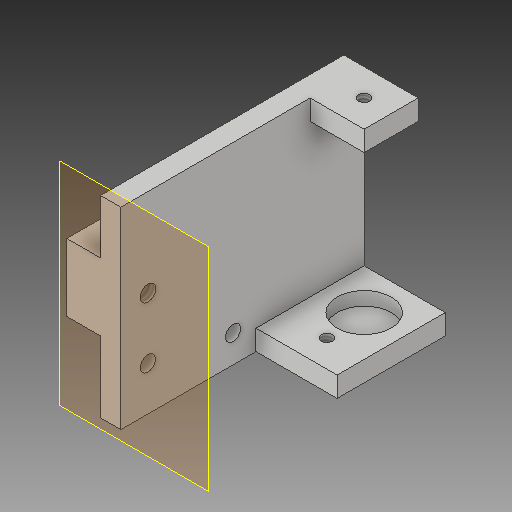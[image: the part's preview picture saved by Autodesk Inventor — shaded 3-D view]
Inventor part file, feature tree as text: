
AUTODESK INVENTOR PART (.ipt)
format: ipt  version: 2017 (Build 210142000, 142)  size: 203,776 bytes
history: native  units: in
note: dims shown in document units (in); Inventor stores cm internally (conversion verified against a paired STEP export)
features: projected_geometry x9, sketch x8, hole x5, extrude x4, plane x1, mirror x1
ambient origin geometry x8: Origin, YZ Plane, XZ Plane, XY Plane, X Axis, Y Axis, Z Axis, Center Point
bodies: Solid1 (feature_tree)
feature tree (28):
  extrude  "Extrusion1"  Depth=2.25in
  extrude  "Extrusion2"  Depth=0.5in
  extrude  "Extrusion3"  Depth=0.5in TaperAngle=0.0deg
  extrude  "Extrusion4"  Depth=0.75in TaperAngle=0.0deg
  hole  "Hole1"  [1 undecoded]
  hole  "Hole2"  [1 undecoded]
  hole  "Hole3"  [1 undecoded]
  hole  "Hole4"  [1 undecoded]
  plane  "Work Plane1"
  mirror  "Mirror1"
  hole  "Hole5"  [1 undecoded]
  sketch  "Sketch1"  dims[d0=1.7812in d1=2.25in]
  sketch  "Sketch2"  dims[d2=0.1875in d3=0.0in d4=0.5in]
  projected_geometry  "Projected Loop1"
  sketch  "Sketch3"  dims[d5=0.1875in d6=0.5in d7=0.0in]
  projected_geometry  "Projected Loop2"
  projected_geometry  "Projected Loop3"
  sketch  "Sketch5"  dims[d8=0.1875in d9=0.75in d10=0.0in]
  projected_geometry  "Projected Loop4"
  projected_geometry  "Projected Loop5"
  sketch  "Sketch6"  dims[d13=0.3125in d14=0.0in d15=0.1875in]
  projected_geometry  "Projected Loop6"
  sketch  "Sketch10"  dims[d16=0.8125in d17=0.25in]
  projected_geometry  "Projected Loop10"
  sketch  "Sketch11"  dims[d18=0.145in d19=0.38in d20=0.375in d21=0.25in d22=0.5635in d23=0.588in d24=0.8108in d25=0.375in]
  projected_geometry  "Projected Loop11"
  sketch  "Sketch12"  dims[d26=0.375in d27=0.5in d28=0.75in d29=0.375in d30=0.25in d31=0.5635in d32=0.125in d33=0.0in d48=0.625in d49=0.5in d50=0.5in d51=0.104in d52=0.276in d53=0.375in d54=0.25in d55=0.5635in d56=0.432in d57=0.8108in d58=0.25in d59=0.104in d60=0.276in d61=0.375in d62=0.25in d63=0.5635in d64=0.432in d65=0.8108in d66=0.406in d67=0.25in d68=0.256in d69=1.0375in d70=0.14in d71=0.75in d72=0.375in d73=0.25in d74=0.5635in d75=1.0in d76=0.8108in]
  projected_geometry  "Projected Loop12"
note: 5 required parameter values undecoded (feature->parameter linkage not recoverable at this tier; creation-order binding heuristic only, values carry confidence <= 0.55)
